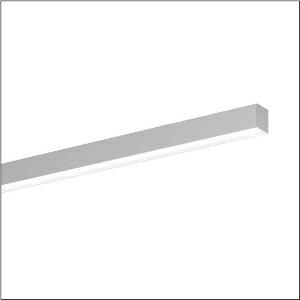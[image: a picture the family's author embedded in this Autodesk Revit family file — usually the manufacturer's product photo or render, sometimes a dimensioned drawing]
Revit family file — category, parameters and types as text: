
# Revit family: silica_r__21_51mx20dc45sb_4e07
name_source: partatom
category: Lighting Fixtures
units: mm (PartAtom-declared; Revit-internal decimal feet)

## family parameters
Cut with Voids When Loaded = No
Host = Face
Light Source = No
Part Type = Normal
Room Calculation Point = No
Round Connector Dimension = Use Diameter
Shared = No

## types (1)
- --- (1 x LED, 6000 lm, 40.1 W, 4000K)
    Apparent Load = 40 VA
    CIE Flux Codes = 48 79 96 100 100
    Color Rendering = 80
    Color Temperature = 4000K
    Default Elevation = 1800 mm
    Description = Silica® 21, office luminaire, primary optical cover: cover, of PMMA, opal, light emission: direct distribution, primary light characteristic: symmetric, installation type: surface-mounted, LED, rated luminous flux: 6.000lm, luminous efficacy: 150lm/W, light colour: 840, colour temperature: 4000K, with terminal, 3+2-pole, max. 2.5mm², mains connection: 220..240V, AC, 50/60Hz, rated input power: 40.1W, luminaire housing, of aluminium, metallic grey (RAL 9006), length: 3.004mm, width: 53mm, height: 53mm, protection rating (complete): IP20, insulation class (complete): insulation class I (protective earthing), certification: CE, permissible operating ambient temperature: 0..+35°C, standard: EN 50419, packaging unit: 1 piece
    Height = 0 mm  [stored 0 ft]
    Lamp = 1 x LED
    Lamp Light Flux = 6000 lm
    Lamp Power = 40.1 W
    Lamp count = 1
    Length = 3004 mm
    Luminous efficacy = 150 lm/W
    Manufacturer = Siteco
    ModVariant = No
    Model = 51MX20DC45SB
    Mounting Place = Ceiling
    Mounting Type = Recessed
    Number of Poles = 1
    OnlyDefault = Yes
    Power Factor = 1
    Product Name = Silica® 21
    Product group = office luminaire | ceiling recessed
    ProductGroupID = 400
    Protection Class = Protection class I
    Protection Degree = IP 20
    RLX_Detail_Level = 1
    RLX_Emergency_Light_Flux = 0 lm
    RLX_Emergency_Type = 0
    RLX_Emergency_Type_DB = No
    RlxData = <blob elided: 26373 chars, md5=70db5dc2>
    Socket = socket
    Standby Power = 0 W
    System Light Flux = 6000 lm
    System Power = 40 W
    Type Comments = factory setting: luminous flux: 100 % | dim-lin: 254 | 218 mA
    Type Image = l_1335933.jpg
    URL = http://relux.com
    VarID = @adj_086687
    Voltage = 0 V
    Weight = 0.00 kg
    Width = 53 mm

note: [stored X ft] marks values corroborated as IEEE doubles in the binary element streams (Revit-internal decimal feet)

## geometry (parser evidence)
native form markers: Blend x4, Sweep x11
no freeform markers — native parametric forms only
